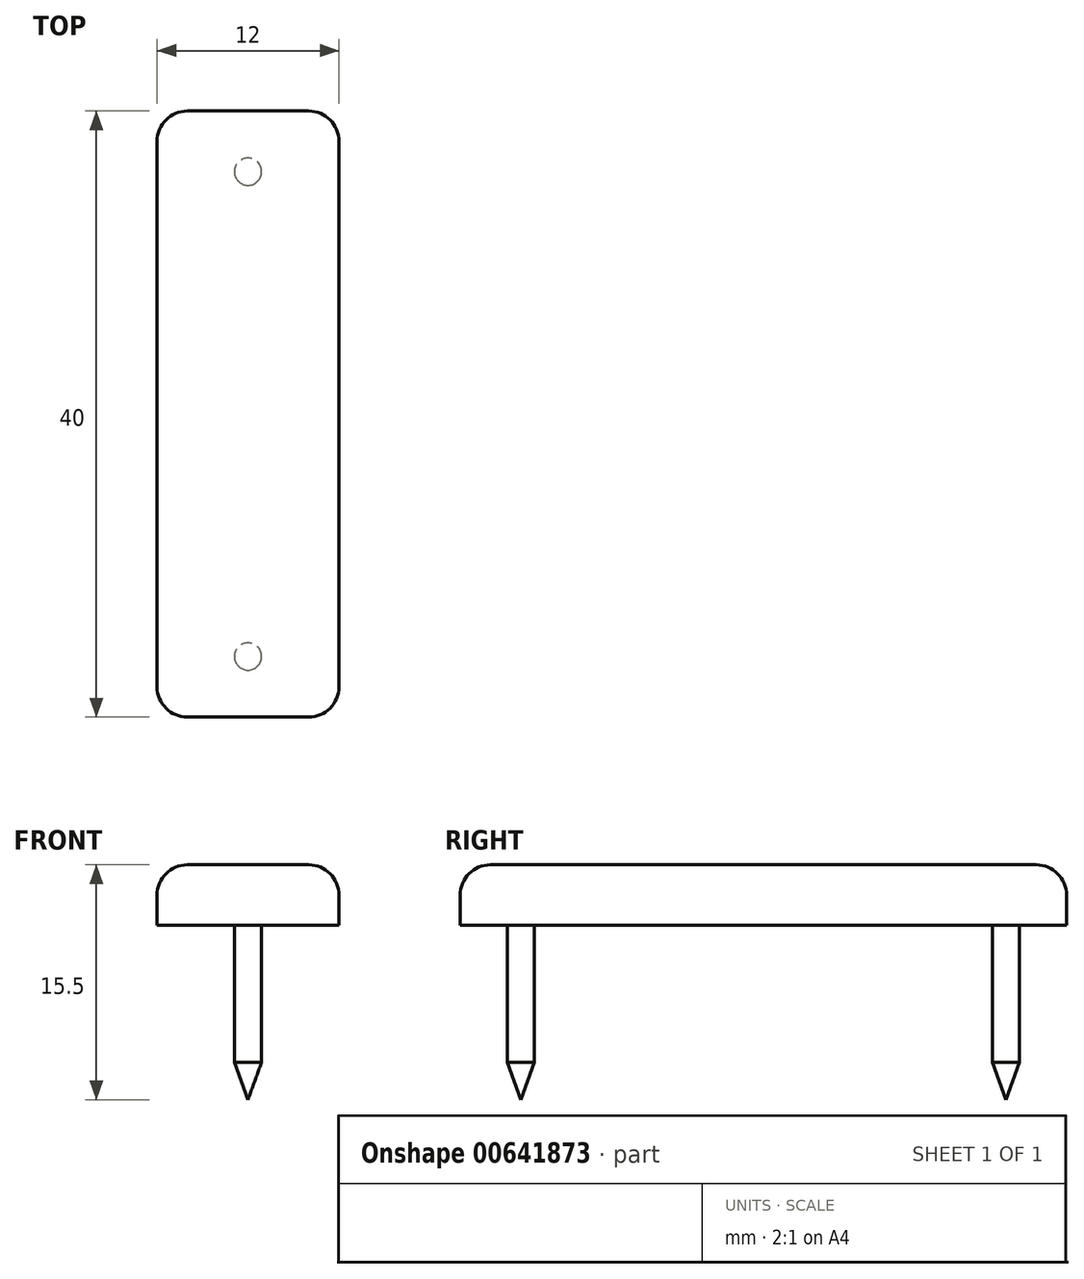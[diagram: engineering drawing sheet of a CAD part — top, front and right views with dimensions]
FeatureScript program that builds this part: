
annotation { "Feature Type Name" : "Feature", "Feature Type Description" : "" }
export const myFeature = defineFeature(function(context is Context, id is Id, definition is map)
    precondition{}
    {
        {
            assignVariable(context, id + "F0", {"name" : "d_d", "anyValue" : 1.8});
        }
        {
            assignVariable(context, id + "F1", {"name" : "H", "anyValue" : 15.5});
        }
        {
            assignVariable(context, id + "F2", {"name" : "h", "anyValue" : 4});
        }
        {
            var Q0;
            Q0=qCreatedBy(makeId("Top.planeOp"),FACE);
            var sketch = newSketch(context, id + "F3", { "sketchPlane" : qUnion([Q0])});
            skLineSegment(sketch, "E0.bottom", {"start": v(-6, -20) * mm, "end": v(6, -20) * mm});
            skLineSegment(sketch, "E0.top", {"start": v(-6, 20) * mm, "end": v(6, 20) * mm});
            skLineSegment(sketch, "E0.left", {"start": v(-6, -20) * mm, "end": v(-6, 20) * mm});
            skLineSegment(sketch, "E0.right", {"start": v(6, -20) * mm, "end": v(6, 20) * mm});
            skLineSegment(sketch, "E1", {"start": v(-6, 0) * mm, "end": v(6, 0) * mm, "construction": true});
            skLineSegment(sketch, "E2", {"start": v(0, 20) * mm, "end": v(0, -20) * mm, "construction": true});
            skSolve(sketch);
        }
        {
            var Q0;
            Q0=makeQuery(id+"F3.imprint","IMPRINT",FACE,{"disambiguationData":[TD([[makeQuery(id+"F3.imprint","IMPRINT",EDGE,{"derivedFrom":sQuery(id+"F3.wireOp",EDGE,"E0.bottom")}),1.0]])]});
            extrude(context, id + "F4", {"entities" : qUnion([Q0]), "depth" : (getVariable(context, 'h')) * mm});
        }
        {
            var Q0;
            Q0=makeQuery(id+"F4.opExtrude","CAP_EDGE",EDGE,{"disambiguationData":[OSD([sQuery(id+"F3.wireOp",EDGE,"E0.right")])],"isStart":false});
            var Q1;
            Q1=makeQuery(id+"F4.opExtrude","CAP_EDGE",EDGE,{"disambiguationData":[OSD([sQuery(id+"F3.wireOp",EDGE,"E0.left")])],"isStart":false});
            var Q2;
            Q2=makeQuery(id+"F4.opExtrude","CAP_EDGE",EDGE,{"disambiguationData":[OSD([sQuery(id+"F3.wireOp",EDGE,"E0.bottom")])],"isStart":false});
            var Q3;
            Q3=makeQuery(id+"F4.opExtrude","SWEPT_EDGE",EDGE,{"disambiguationData":[OSD([sQuery(id+"F3.wireOp",EDGE,"E0.bottom"),sQuery(id+"F3.wireOp",EDGE,"E0.right")])]});
            var Q4;
            Q4=makeQuery(id+"F4.opExtrude","SWEPT_EDGE",EDGE,{"disambiguationData":[OSD([sQuery(id+"F3.wireOp",EDGE,"E0.top"),sQuery(id+"F3.wireOp",EDGE,"E0.left")])]});
            var Q5;
            Q5=makeQuery(id+"F4.opExtrude","SWEPT_EDGE",EDGE,{"disambiguationData":[OSD([sQuery(id+"F3.wireOp",EDGE,"E0.top"),sQuery(id+"F3.wireOp",EDGE,"E0.right")])]});
            var Q6;
            Q6=makeQuery(id+"F4.opExtrude","CAP_EDGE",EDGE,{"disambiguationData":[OSD([sQuery(id+"F3.wireOp",EDGE,"E0.top")])],"isStart":false});
            var Q7;
            Q7=makeQuery(id+"F4.opExtrude","SWEPT_EDGE",EDGE,{"disambiguationData":[OSD([sQuery(id+"F3.wireOp",EDGE,"E0.bottom"),sQuery(id+"F3.wireOp",EDGE,"E0.left")])]});
            fillet(context, id + "F5", {"entities" : qUnion([Q0, Q1, Q2, Q3, Q4, Q5, Q6, Q7]), "radius" : 2 * mm, "tangentPropagation" : true, "allowEdgeOverflow" : false});
        }
        {
            var Q0;
            Q0=makeQuery(id+"F4.opExtrude","CAP_FACE",FACE,{"disambiguationData":[OSD([sQuery(id+"F3.wireOp",EDGE,"E0.bottom"),sQuery(id+"F3.wireOp",EDGE,"E0.top"),sQuery(id+"F3.wireOp",EDGE,"E0.left"),sQuery(id+"F3.wireOp",EDGE,"E0.right")])],"isStart":true});
            var sketch = newSketch(context, id + "F6", { "sketchPlane" : qUnion([Q0])});
            skCircle(sketch, "E3", {"center": v(0, -16) * mm, "radius": 0.9 * mm});
            skCircle(sketch, "E4", {"center": v(0, 16) * mm, "radius": 0.9 * mm});
            skLineSegment(sketch, "E5", {"start": v(0, -16) * mm, "end": v(0, 16) * mm, "construction": true});
            skSolve(sketch);
        }
        {
            var Q0;
            Q0=makeQuery(id+"F6.imprint","IMPRINT",FACE,{"disambiguationData":[TD([[makeQuery(id+"F6.imprint","IMPRINT",EDGE,{"derivedFrom":sQuery(id+"F6.wireOp",EDGE,"E3")}),1.0]])]});
            var Q1;
            Q1=makeQuery(id+"F6.imprint","IMPRINT",FACE,{"disambiguationData":[TD([[makeQuery(id+"F6.imprint","IMPRINT",EDGE,{"derivedFrom":sQuery(id+"F6.wireOp",EDGE,"E4")}),1.0]])]});
            var Q2;
            Q2=sQuery(id+"F6.wireOp",EDGE,"E3");
            var Q3;
            Q3=sQuery(id+"F6.wireOp",EDGE,"E4");
            extrude(context, id + "F7", {"entities" : qUnion([Q0, Q1]), "operationType" : NewBodyOperationType.ADD, "surfaceEntities" : qUnion([Q2, Q3]), "depth" : (getVariable(context, 'H') - getVariable(context, 'h')) * mm});
        }
        {
            var Q0;
            Q0=makeQuery(id+"F7.opExtrude","CAP_EDGE",EDGE,{"disambiguationData":[OSD([sQuery(id+"F6.wireOp",EDGE,"E3")])],"isStart":false});
            var Q1;
            Q1=makeQuery(id+"F7.opExtrude","CAP_EDGE",EDGE,{"disambiguationData":[OSD([sQuery(id+"F6.wireOp",EDGE,"E4")])],"isStart":false});
            chamfer(context, id + "F8", {"entities" : qUnion([Q0, Q1]), "chamferType" : ChamferType.OFFSET_ANGLE, "width" : (getVariable(context, 'd_d') / 2) * mm, "oppositeDirection" : false, "angle" : 70 * degree, "tangentPropagation" : true});
        }
    });
